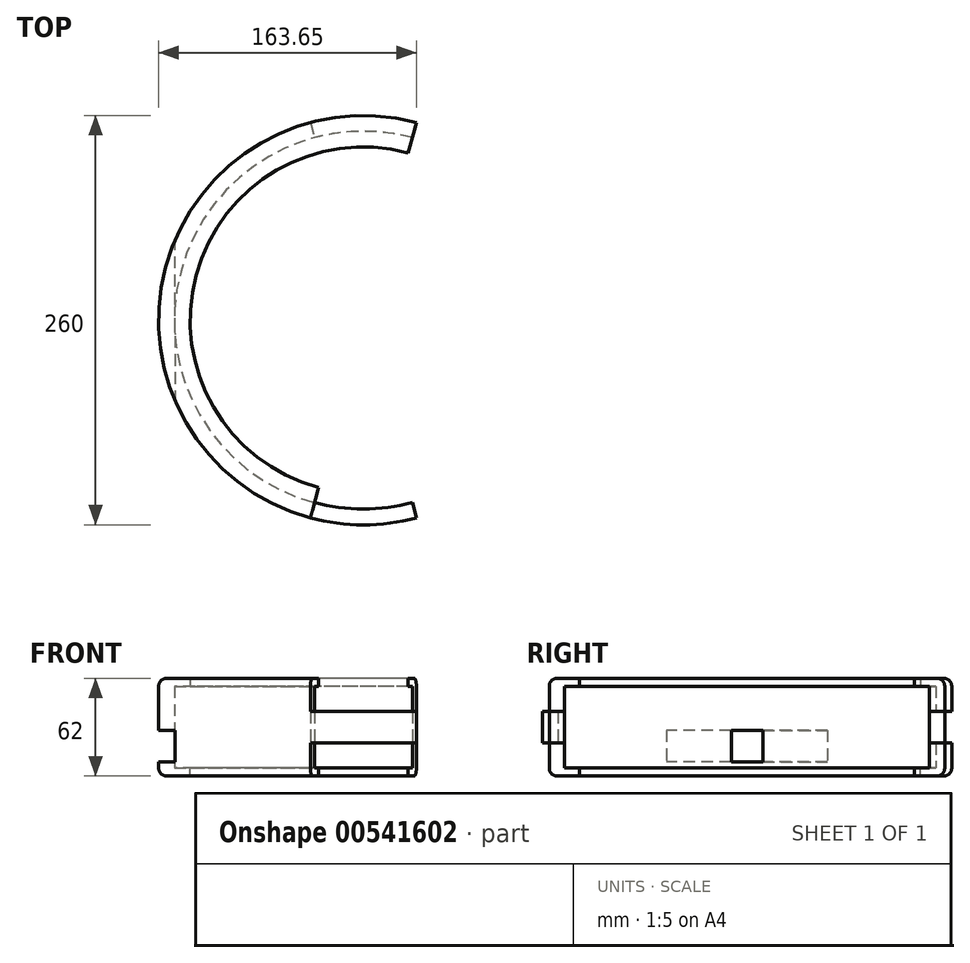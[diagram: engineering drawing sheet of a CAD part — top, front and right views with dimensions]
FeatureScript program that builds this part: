
annotation { "Feature Type Name" : "Feature", "Feature Type Description" : "" }
export const myFeature = defineFeature(function(context is Context, id is Id, definition is map)
    precondition{}
    {
        {
            var Q0;
            Q0=qCreatedBy(makeId("Top.planeOp"),FACE);
            var sketch = newSketch(context, id + "F0", { "sketchPlane" : qUnion([Q0])});
            skArc(sketch, "E0", {"start": v(31.06, 115.91) * mm, "mid": v(-120, 0) * mm, "end": v(31.06, -115.91) * mm});
            skArc(sketch, "E1", {"start": v(33.65, 125.57) * mm, "mid": v(-130, 0) * mm, "end": v(33.65, -125.57) * mm});
            skLineSegment(sketch, "E2", {"start": v(33.65, 125.57) * mm, "end": v(31.06, 115.91) * mm});
            skLineSegment(sketch, "E3", {"start": v(31.06, -115.91) * mm, "end": v(33.65, -125.57) * mm});
            skLineSegment(sketch, "E4", {"start": v(0, 0) * mm, "end": v(38.11, -142.23) * mm, "construction": true});
            skLineSegment(sketch, "E5", {"start": v(0, 0) * mm, "end": v(33.65, 125.57) * mm, "construction": true});
            skSolve(sketch);
        }
        {
            var Q0;
            Q0 = qSketchRegion(id + "F0", true);
            extrude(context, id + "F1", {"entities" : qUnion([Q0]), "depth" : 26 * mm, "offsetDistance" : 25 * mm, "hasSecondDirection" : true, "secondDirectionOppositeDirection" : true, "secondDirectionDepth" : 26 * mm});
        }
        {
            var Q0;
            Q0=makeQuery(id+"F1.opExtrude","CAP_FACE",FACE,{"disambiguationData":[OSD([sQuery(id+"F0.wireOp",EDGE,"E0"),sQuery(id+"F0.wireOp",EDGE,"E1"),sQuery(id+"F0.wireOp",EDGE,"E2"),sQuery(id+"F0.wireOp",EDGE,"E3")])],"isStart":false});
            var sketch = newSketch(context, id + "F2", { "sketchPlane" : qUnion([Q0])});
            skArc(sketch, "E6", {"start": v(33.65, 125.57) * mm, "mid": v(-130, 0) * mm, "end": v(33.65, -125.57) * mm});
            skArc(sketch, "E7", {"start": v(28.47, 106.25) * mm, "mid": v(-110, 0) * mm, "end": v(28.47, -106.25) * mm});
            skLineSegment(sketch, "E8", {"start": v(33.65, 125.57) * mm, "end": v(28.47, 106.25) * mm});
            skLineSegment(sketch, "E9", {"start": v(28.47, -106.25) * mm, "end": v(33.65, -125.57) * mm});
            skLineSegment(sketch, "E10", {"start": v(0, 0) * mm, "end": v(31.06, 115.91) * mm, "construction": true});
            skLineSegment(sketch, "E11", {"start": v(0, 0) * mm, "end": v(31.06, -115.91) * mm, "construction": true});
            skSolve(sketch);
        }
        {
            var Q0;
            Q0 = qSketchRegion(id + "F2", true);
            extrude(context, id + "F3", {"entities" : qUnion([Q0]), "operationType" : NewBodyOperationType.ADD, "depth" : 5 * mm, "offsetDistance" : 25 * mm});
        }
        {
            var Q0;
            Q0=makeQuery(id+"F1.opExtrude","CAP_FACE",FACE,{"disambiguationData":[OSD([sQuery(id+"F0.wireOp",EDGE,"E0"),sQuery(id+"F0.wireOp",EDGE,"E1"),sQuery(id+"F0.wireOp",EDGE,"E2"),sQuery(id+"F0.wireOp",EDGE,"E3")])],"isStart":true});
            var sketch = newSketch(context, id + "F4", { "sketchPlane" : qUnion([Q0])});
            skArc(sketch, "E12", {"start": v(33.65, 125.57) * mm, "mid": v(-130, 0) * mm, "end": v(33.65, -125.57) * mm});
            skLineSegment(sketch, "E13", {"start": v(0, 0) * mm, "end": v(33.65, 125.57) * mm, "construction": true});
            skLineSegment(sketch, "E14", {"start": v(0, 0) * mm, "end": v(33.65, -125.57) * mm, "construction": true});
            skArc(sketch, "E15", {"start": v(28.47, 106.25) * mm, "mid": v(-110, 0) * mm, "end": v(28.47, -106.25) * mm});
            skLineSegment(sketch, "E16", {"start": v(33.65, 125.57) * mm, "end": v(28.47, 106.25) * mm});
            skLineSegment(sketch, "E17", {"start": v(28.47, -106.25) * mm, "end": v(33.65, -125.57) * mm});
            skSolve(sketch);
        }
        {
            var Q0;
            Q0 = qSketchRegion(id + "F4", true);
            extrude(context, id + "F5", {"entities" : qUnion([Q0]), "operationType" : NewBodyOperationType.ADD, "depth" : 5 * mm, "offsetDistance" : 25 * mm});
        }
        {
            var Q0;
            Q0=qCreatedBy(makeId("Top.planeOp"),FACE);
            var sketch = newSketch(context, id + "F6", { "sketchPlane" : qUnion([Q0])});
            skLineSegment(sketch, "E18", {"start": v(0, 0) * mm, "end": v(35.72, 133.3) * mm, "construction": true});
            skLineSegment(sketch, "E19", {"start": v(0, 0) * mm, "end": v(-35.82, 133.67) * mm, "construction": true});
            skArc(sketch, "E20", {"start": v(34.27, 127.92) * mm, "mid": v(0, 132.43) * mm, "end": v(-34.27, 127.92) * mm});
            skArc(sketch, "E21", {"start": v(27.8, 103.74) * mm, "mid": v(0, 107.25) * mm, "end": v(-27.8, 103.74) * mm});
            skLineSegment(sketch, "E22", {"start": v(34.27, 127.92) * mm, "end": v(27.8, 103.74) * mm});
            skLineSegment(sketch, "E23", {"start": v(-34.27, 127.92) * mm, "end": v(-27.8, 103.74) * mm});
            skSolve(sketch);
        }
        {
            var Q0;
            Q0 = qSketchRegion(id + "F6", true);
            extrude(context, id + "F7", {"entities" : qUnion([Q0]), "operationType" : NewBodyOperationType.REMOVE, "oppositeDirection" : true, "depth" : 10 * mm, "offsetDistance" : 25 * mm, "hasSecondDirection" : true, "secondDirectionOppositeDirection" : false, "secondDirectionDepth" : 10 * mm});
        }
        {
            var Q0;
            Q0=makeQuery(id+"F3.opExtrude","CAP_FACE",FACE,{"disambiguationData":[OSD([sQuery(id+"F2.wireOp",EDGE,"E6"),sQuery(id+"F2.wireOp",EDGE,"E7"),sQuery(id+"F2.wireOp",EDGE,"E8"),sQuery(id+"F2.wireOp",EDGE,"E9")])],"isStart":false});
            var sketch = newSketch(context, id + "F8", { "sketchPlane" : qUnion([Q0])});
            skLineSegment(sketch, "E24", {"start": v(0, 0) * mm, "end": v(38.37, -143.2) * mm, "construction": true});
            skLineSegment(sketch, "E25", {"start": v(0, 0) * mm, "end": v(-38.59, -144.01) * mm, "construction": true});
            skArc(sketch, "E26", {"start": v(-27.15, -101.34) * mm, "mid": v(0, -104.92) * mm, "end": v(27.15, -101.34) * mm});
            skArc(sketch, "E27", {"start": v(36.16, -134.95) * mm, "mid": v(0, -139.7) * mm, "end": v(-36.16, -134.95) * mm});
            skLineSegment(sketch, "E28", {"start": v(-27.15, -101.34) * mm, "end": v(-36.16, -134.95) * mm});
            skLineSegment(sketch, "E29", {"start": v(27.15, -101.34) * mm, "end": v(36.16, -134.95) * mm});
            skSolve(sketch);
        }
        {
            var Q0;
            Q0 = qSketchRegion(id + "F8", true);
            extrude(context, id + "F9", {"entities" : qUnion([Q0]), "operationType" : NewBodyOperationType.REMOVE, "oppositeDirection" : true, "depth" : 21 * mm, "offsetDistance" : 25 * mm});
        }
        {
            var Q0;
            Q0=makeQuery(id+"F5.opExtrude","CAP_FACE",FACE,{"disambiguationData":[OSD([sQuery(id+"F4.wireOp",EDGE,"E12"),sQuery(id+"F4.wireOp",EDGE,"E15"),sQuery(id+"F4.wireOp",EDGE,"E16"),sQuery(id+"F4.wireOp",EDGE,"E17")])],"isStart":false});
            var sketch = newSketch(context, id + "F10", { "sketchPlane" : qUnion([Q0])});
            skLineSegment(sketch, "E30", {"start": v(0, 0) * mm, "end": v(-38.37, 143.2) * mm, "construction": true});
            skLineSegment(sketch, "E31", {"start": v(0, 0) * mm, "end": v(38.59, 144.01) * mm, "construction": true});
            skArc(sketch, "E32", {"start": v(27.15, 101.34) * mm, "mid": v(0, 104.92) * mm, "end": v(-27.15, 101.34) * mm});
            skArc(sketch, "E33", {"start": v(-36.16, 134.95) * mm, "mid": v(0, 139.7) * mm, "end": v(36.16, 134.95) * mm});
            skLineSegment(sketch, "E34", {"start": v(27.15, 101.34) * mm, "end": v(36.16, 134.95) * mm});
            skLineSegment(sketch, "E35", {"start": v(-27.15, 101.34) * mm, "end": v(-36.16, 134.95) * mm});
            skSolve(sketch);
        }
        {
            var Q0;
            Q0 = qSketchRegion(id + "F10", true);
            extrude(context, id + "F11", {"entities" : qUnion([Q0]), "operationType" : NewBodyOperationType.REMOVE, "oppositeDirection" : true, "depth" : 21 * mm, "offsetDistance" : 25 * mm});
        }
        {
            var Q0;
            Q0=makeQuery(id+"F3.opExtrude","CAP_EDGE",EDGE,{"disambiguationData":[OSD([sQuery(id+"F2.wireOp",EDGE,"E6")])],"isStart":false});
            var Q1;
            Q1=makeQuery(id+"F5.opExtrude","CAP_EDGE",EDGE,{"disambiguationData":[OSD([sQuery(id+"F4.wireOp",EDGE,"E12")])],"isStart":false});
            fillet(context, id + "F12", {"entities" : qUnion([Q0, Q1]), "radius" : 5 * mm, "tangentPropagation" : true, "allowEdgeOverflow" : false});
        }
        {
            var Q0;
            Q0=qCreatedBy(makeId("Right.planeOp"),FACE);
            cPlane(context, id + "F13", {"entities" : qUnion([Q0]), "cplaneType" : CPlaneType.OFFSET, "offset" : 130 * mm, "oppositeDirection" : true, "width" : 150 * mm, "height" : 150 * mm});
        }
        {
            var Q0;
            Q0=qCreatedBy(id+"F13.planeOp",FACE);
            var sketch = newSketch(context, id + "F14", { "sketchPlane" : qUnion([Q0])});
            skLineSegment(sketch, "E36.bottom", {"start": v(-10, -22) * mm, "end": v(10, -22) * mm});
            skLineSegment(sketch, "E36.top", {"start": v(-10, -2) * mm, "end": v(10, -2) * mm});
            skLineSegment(sketch, "E36.left", {"start": v(-10, -22) * mm, "end": v(-10, -2) * mm});
            skLineSegment(sketch, "E36.right", {"start": v(10, -22) * mm, "end": v(10, -2) * mm});
            skPoint(sketch, "E36.middle", {"position": v(0, -12) * mm});
            skSolve(sketch);
        }
        {
            var Q0;
            Q0 = qSketchRegion(id + "F14", true);
            extrude(context, id + "F15", {"entities" : qUnion([Q0]), "operationType" : NewBodyOperationType.REMOVE, "depth" : 17.6 * mm, "offsetDistance" : 25 * mm});
        }
        {
            var Q0;
            Q0=makeQuery(id+"F15.boolean.opBoolean","COPY",FACE,{"derivedFrom":makeQuery(id+"F15.opExtrude","SWEPT_FACE",FACE,{"disambiguationData":[OSD([sQuery(id+"F14.wireOp",EDGE,"E36.bottom")])]})});
            var sketch = newSketch(context, id + "F16", { "sketchPlane" : qUnion([Q0])});
            skLineSegment(sketch, "E37", {"start": v(-119.58, 10) * mm, "end": v(-119.58, 54.31) * mm});
            skLineSegment(sketch, "E38", {"start": v(-119.58, 54.31) * mm, "end": v(-136.4, 54.31) * mm});
            skLineSegment(sketch, "E39", {"start": v(-119.58, -10) * mm, "end": v(-119.58, -56.91) * mm});
            skLineSegment(sketch, "E40", {"start": v(-119.58, -56.91) * mm, "end": v(-136.82, -56.91) * mm});
            skLineSegment(sketch, "E41", {"start": v(-136.82, -56.91) * mm, "end": v(-136.4, 54.31) * mm});
            skLineSegment(sketch, "E42", {"start": v(-119.58, 10) * mm, "end": v(-134.3, 0) * mm});
            skLineSegment(sketch, "E43", {"start": v(-134.3, 0) * mm, "end": v(-119.58, -10) * mm});
            skSolve(sketch);
        }
        {
            var Q0;
            Q0 = qSketchRegion(id + "F16", true);
            extrude(context, id + "F17", {"entities" : qUnion([Q0]), "operationType" : NewBodyOperationType.REMOVE, "depth" : 20 * mm, "offsetDistance" : 25 * mm});
        }
    });
